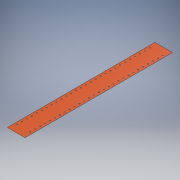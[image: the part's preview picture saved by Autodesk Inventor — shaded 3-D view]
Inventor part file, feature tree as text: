
AUTODESK INVENTOR PART (.ipt)
format: ipt  version: 2019 (Build 230136000, 136)  size: 218,624 bytes
history: native  units: mm
features: extrude x2, other x2, mirror x1
ambient origin geometry x8: Origin, YZ Plane, XZ Plane, XY Plane, X Axis, Y Axis, Z Axis, Center Point
bodies: Body1 (feature_tree)
feature tree (5):
  extrude  "Skin Body"  Depth=1513.0mm
  extrude  "End Cut"  Depth=756.5mm
  mirror  "End Cut Mirror"
  other  "Skin Scheme"
  other  "End Cut Outline"
